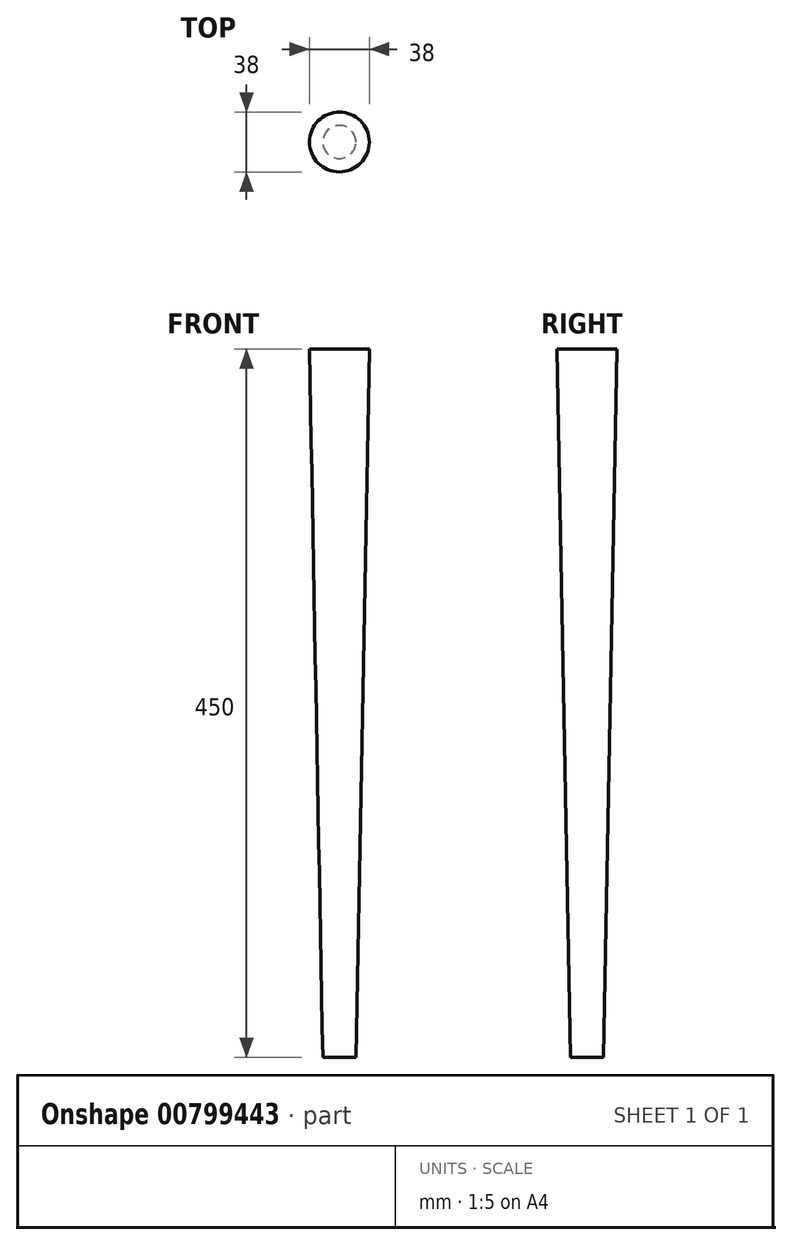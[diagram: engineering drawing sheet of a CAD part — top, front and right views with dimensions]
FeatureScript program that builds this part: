
annotation { "Feature Type Name" : "Feature", "Feature Type Description" : "" }
export const myFeature = defineFeature(function(context is Context, id is Id, definition is map)
    precondition{}
    {
        {
            var Q0;
            Q0=qCreatedBy(makeId("Front.planeOp"),FACE);
            var sketch = newSketch(context, id + "F0", { "sketchPlane" : qUnion([Q0])});
            skLineSegment(sketch, "E0", {"start": v(0, 0) * mm, "end": v(10.5, 0) * mm});
            skLineSegment(sketch, "E1", {"start": v(0, 0) * mm, "end": v(0, 450) * mm});
            skLineSegment(sketch, "E2", {"start": v(0, 450) * mm, "end": v(19, 450) * mm});
            skLineSegment(sketch, "E3", {"start": v(19, 450) * mm, "end": v(10.5, 0) * mm});
            skSolve(sketch);
        }
        {
            var Q0;
            Q0=makeQuery(id+"F0.imprint","IMPRINT",FACE,{"disambiguationData":[TD([[makeQuery(id+"F0.imprint","IMPRINT",EDGE,{"derivedFrom":sQuery(id+"F0.wireOp",EDGE,"E0")}),1.0]])]});
            var Q1;
            Q1=sQuery(id+"F0.wireOp",EDGE,"E1");
            revolve(context, id + "F1", {"entities" : qUnion([Q0]), "axis" : qUnion([Q1]), "revolveType" : RevolveType.FULL});
        }
    });
